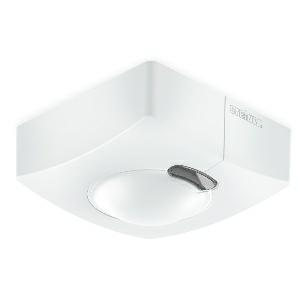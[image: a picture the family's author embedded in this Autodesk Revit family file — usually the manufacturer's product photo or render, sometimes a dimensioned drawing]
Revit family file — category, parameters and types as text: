
# Revit family: hf_3360_011734
name_source: partatom
category: Elektroinstallationen
revit_build: Autodesk Revit 2016 (Build: 20190508_0715(x64)
units: mm (PartAtom-declared; Revit-internal decimal feet)

## family parameters
Basisbauteil = Fläche
Beim Laden mit Abzugskörper schneiden = Nein
Bemaßung runder Anschluss = Durchmesser verwenden
Beschriftungsausrichtung beibehalten = Nein
Gemeinsam genutzt = Nein
Raumberechnungspunkt = Nein
Teiletyp = Normal

## types (1)
- HF 3360
    Apparent Load = 0 VA
    Beschreibung = Type: Motion detectors; Dimensions (L x W x H): 52 x 95 x 95 mm; Mains power supply: 220 – 240 V / 50 – 60 Hz; Sensor Technology: High frequency; Application, place: Indoors; Application, room: function room / ancillary room, stairwell, WC / washroom, multi-storey / underground car park, Indoors; Installation site: wall, ceiling, corner; Installation: Surface wiring; HF-system: 5,8 GHz; Electronic scalability: Yes; Mechanical scalability: No; Mounting height: 2,00 – 4,00 m; Optimum mounting height: 2,8 m; Detection: also through glass, wood and stud walls; Detection angle: 360 °; Angle of aperture: 140 °; Sneak-by guard: Yes; Reach, radial: Ø 8 m (50 m²); Reach, tangential: Ø 8 m (50 m²); Twilight setting TEACH: Yes; Twilight setting: 2 – 1000 lx; Time setting: 5 sec – 15 min; Switching output 1, resistive: 2000 W; Switching output 1, number of LEDs / fluorescent lamps: 8 pcs.; Constant-lighting control: No; Basic light level function: No; Functions: Normal / test mode, Manual ON / ON-OFF; Settings via: Remote control, Potentiometers, Smart Remote; With remote control: No; Interconnection: Yes; IP-rating: IP54; Material: Plastic; Ambient temperature: -20 – 50 °C; Colour: white; Colour, RAL: 9003; Manufacturer's Warranty: 5 years; Version: COM1 - surface, sq.; PU1, EAN: 4007841011734
    Height = 95 mm
    Hersteller = Steinel
    Length = 52 mm  [stored 0.170604 ft]
    ModVariant = Nein
    Modell = 011734
    Mounting Type = Surface mounted
    Number of Poles = 1
    OnlyDefault = Ja
    Power Factor = 1
    Product Name = HF 3360
    Product group = Sensor-switched indoor light
    ProductGroupID = 30
    Protection Class = Protection class
    Protection Degree = IP 54
    RlxData = <blob elided: 25961 chars, md5=600aa5fe>
    SensorDataFile = {"IESDataFiles":[]}
    Typenbild = produkt1_011734.jpg
    Typenkommentare = Product without accessories
    URL = http://relux.com
    VarID = ---
    Voltage = 0 V
    Vorgabe-Ansicht = 1800 mm
    Weight = 0.00 kg
    Width = 95 mm

note: [stored X ft] marks values corroborated as IEEE doubles in the binary element streams (Revit-internal decimal feet)

## geometry (parser evidence)
native form markers: Blend x4, Sweep x11
no freeform markers — native parametric forms only
